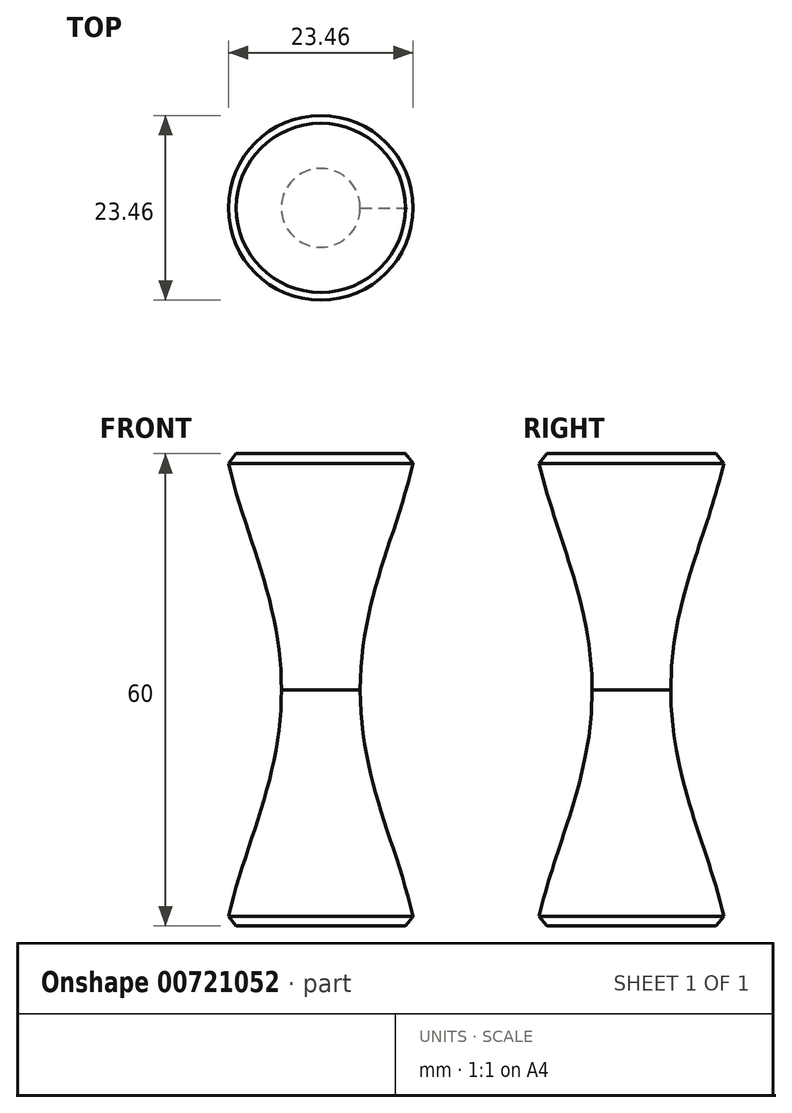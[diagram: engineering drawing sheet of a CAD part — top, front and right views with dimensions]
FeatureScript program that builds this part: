
annotation { "Feature Type Name" : "Feature", "Feature Type Description" : "" }
export const myFeature = defineFeature(function(context is Context, id is Id, definition is map)
    precondition{}
    {
        {
            var Q0;
            Q0=qCreatedBy(makeId("Front.planeOp"),FACE);
            var sketch = newSketch(context, id + "F0", { "sketchPlane" : qUnion([Q0])});
            skLineSegment(sketch, "E0", {"start": v(0, -30) * mm, "end": v(12, -30) * mm});
            skLineSegment(sketch, "E1", {"start": v(0, 0) * mm, "end": v(5, 0) * mm});
            skFitSpline(sketch, "E2", {"points": [v(5, 0) * mm, v(12, -30) * mm], "startDerivative": vector(0, -34.89) * mm, "endDerivative": vector(6.66, -31.45) * mm});
            skLineSegment(sketch, "E3", {"start": v(0, -11.63) * mm, "end": v(5, -11.63) * mm, "construction": true});
            skLineSegment(sketch, "E4", {"start": v(0, 0) * mm, "end": v(0, -30) * mm});
            skSolve(sketch);
        }
        {
            var Q0;
            Q0=makeQuery(id+"F0.imprint","IMPRINT",FACE,{"disambiguationData":[TD([[makeQuery(id+"F0.imprint","IMPRINT",EDGE,{"derivedFrom":sQuery(id+"F0.wireOp",EDGE,"E0")}),1.0]])]});
            var Q1;
            Q1=sQuery(id+"F0.wireOp",EDGE,"E4");
            revolve(context, id + "F1", {"surfaceOperationType" : NewSurfaceOperationType.NEW, "entities" : qUnion([Q0]), "axis" : qUnion([Q1]), "revolveType" : RevolveType.FULL});
        }
        {
            var Q0;
            Q0=makeQuery(id+"F1.opRevolve","SWEPT_EDGE",EDGE,{"disambiguationData":[OSD([sQuery(id+"F0.wireOp",EDGE,"E0"),sQuery(id+"F0.wireOp",EDGE,"E2")])]});
            chamfer(context, id + "F2", {"entities" : qUnion([Q0]), "width" : 1 * mm, "tangentPropagation" : true});
        }
        {
            var Q0;
            Q0=makeQuery(id+"F1.opRevolve","SWEPT_BODY",BODY,{"disambiguationData":[OSD([sQuery(id+"F0.wireOp",EDGE,"E0"),sQuery(id+"F0.wireOp",EDGE,"E1"),sQuery(id+"F0.wireOp",EDGE,"E2"),sQuery(id+"F0.wireOp",EDGE,"E4")])]});
            var Q1;
            Q1=qCreatedBy(makeId("Top.planeOp"),FACE);
            mirror(context, id + "F3", {"operationType" : NewBodyOperationType.ADD, "entities" : qUnion([Q0]), "mirrorPlane" : qUnion([Q1])});
        }
    });
